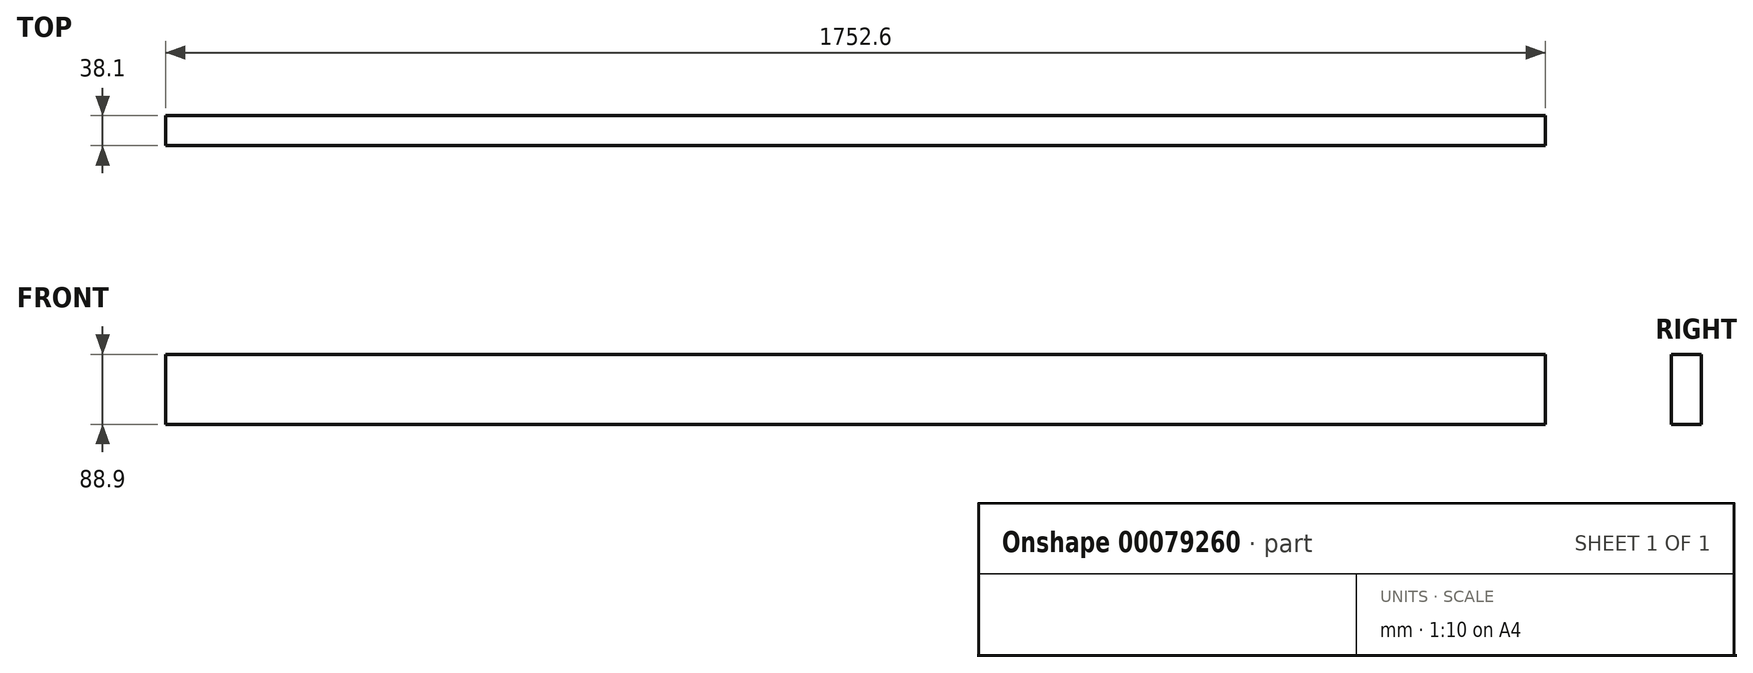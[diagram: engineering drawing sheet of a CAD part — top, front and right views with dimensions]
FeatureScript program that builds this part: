
annotation { "Feature Type Name" : "Feature", "Feature Type Description" : "" }
export const myFeature = defineFeature(function(context is Context, id is Id, definition is map)
    precondition{}
    {
        {
            var Q0;
            Q0=qCreatedBy(makeId("Right.planeOp"),FACE);
            var sketch = newSketch(context, id + "F0", { "sketchPlane" : qUnion([Q0])});
            skLineSegment(sketch, "E0.bottom", {"start": v(0, 0) * mm, "end": v(-38.1, 0) * mm});
            skLineSegment(sketch, "E0.top", {"start": v(0, 88.9) * mm, "end": v(-38.1, 88.9) * mm});
            skLineSegment(sketch, "E0.left", {"start": v(0, 0) * mm, "end": v(0, 88.9) * mm});
            skLineSegment(sketch, "E0.right", {"start": v(-38.1, 0) * mm, "end": v(-38.1, 88.9) * mm});
            skSolve(sketch);
        }
        {
            var Q0;
            Q0=makeQuery(id+"F0.imprint","IMPRINT",FACE,{"disambiguationData":[TD([[makeQuery(id+"F0.imprint","IMPRINT",EDGE,{"derivedFrom":sQuery(id+"F0.wireOp",EDGE,"E0.bottom")}),-1.0]])]});
            extrude(context, id + "F1", {"entities" : qUnion([Q0]), "depth" : 1752.6 * mm});
        }
    });
